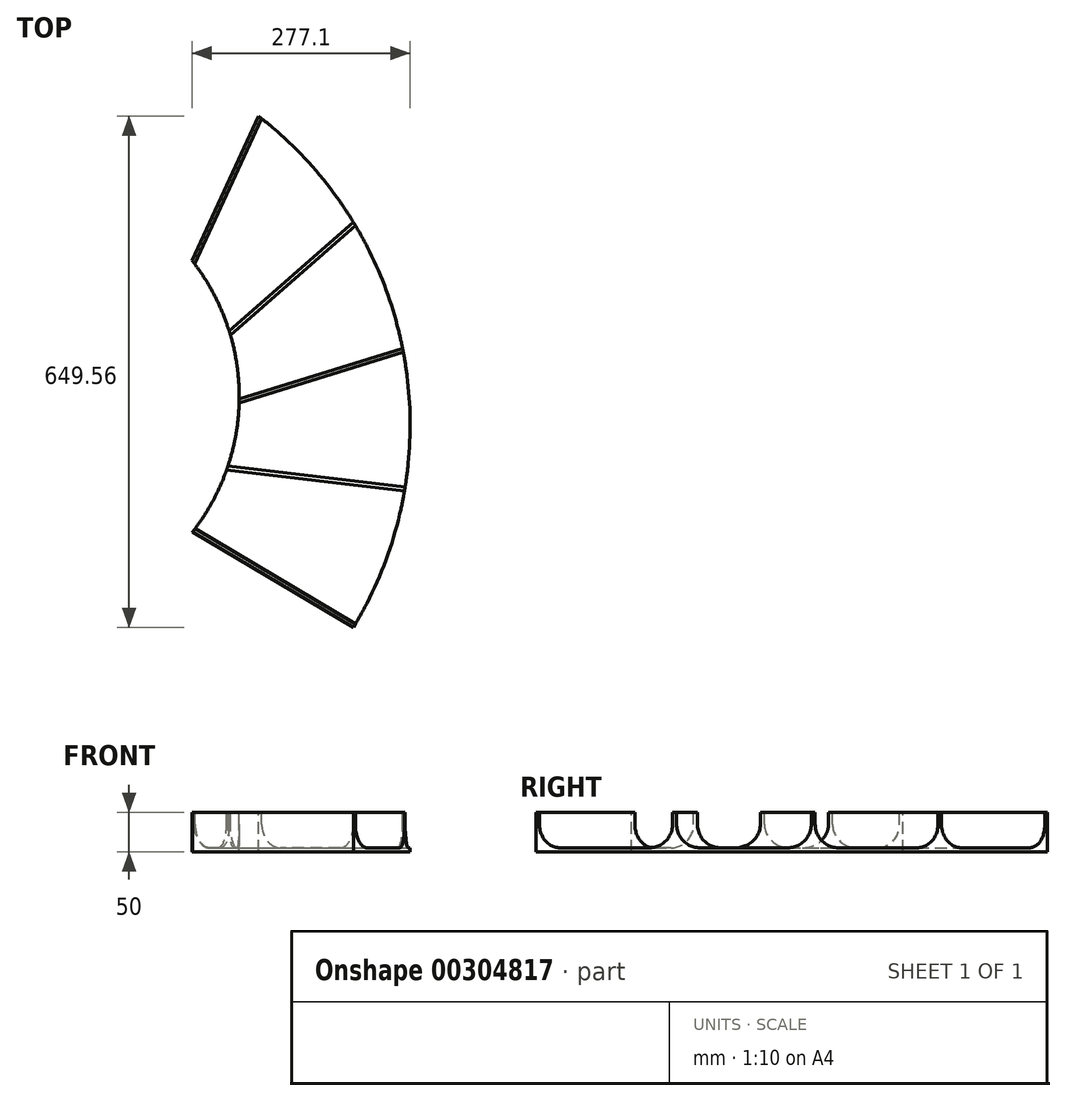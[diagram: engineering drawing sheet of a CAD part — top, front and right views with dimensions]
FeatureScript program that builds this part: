
annotation { "Feature Type Name" : "Feature", "Feature Type Description" : "" }
export const myFeature = defineFeature(function(context is Context, id is Id, definition is map)
    precondition{}
    {
        {
            var Q0;
            Q0=qCreatedBy(makeId("Top.planeOp"),FACE);
            var sketch = newSketch(context, id + "F0", { "sketchPlane" : qUnion([Q0])});
            skLineSegment(sketch, "E0.8.0", {"start": v(150, -96.9) * mm, "end": v(419.17, -128.76) * mm});
            skLineSegment(sketch, "E0.8.1", {"start": v(150, -174.88) * mm, "end": v(356.74, -297.88) * mm});
            skLineSegment(sketch, "E0.9.0", {"start": v(150, -35.73) * mm, "end": v(417.73, 47.4) * mm});
            skLineSegment(sketch, "E0.9.1", {"start": v(150, -91.87) * mm, "end": v(420, -123.83) * mm});
            skLineSegment(sketch, "E0.10.0", {"start": v(150, 27) * mm, "end": v(356.85, 208.4) * mm});
            skLineSegment(sketch, "E0.10.1", {"start": v(150, -30.5) * mm, "end": v(416.77, 52.34) * mm});
            skLineSegment(sketch, "E0.11.0", {"start": v(150, 153.59) * mm, "end": v(237.87, 344.2) * mm});
            skLineSegment(sketch, "E0.11.1", {"start": v(150, 33.65) * mm, "end": v(354.23, 212.75) * mm});
            skArc(sketch, "E1", {"start": v(356.74, -297.88) * mm, "mid": v(418.09, 45.52) * mm, "end": v(237.87, 344.2) * mm});
            skLineSegment(sketch, "E2", {"start": v(233.83, 347.38) * mm, "end": v(149.26, 163.92) * mm});
            skLineSegment(sketch, "E3", {"start": v(150.05, -180.73) * mm, "end": v(354.18, -302.18) * mm});
            skLineSegment(sketch, "E4", {"start": v(237.87, 344.2) * mm, "end": v(233.83, 347.38) * mm});
            skLineSegment(sketch, "E5", {"start": v(356.74, -297.88) * mm, "end": v(354.18, -302.18) * mm});
            skArc(sketch, "E6", {"start": v(150.05, -180.73) * mm, "mid": v(209.25, -8.27) * mm, "end": v(149.26, 163.92) * mm});
            skPoint(sketch, "E7", {"position": v(0, 0) * mm});
            skSolve(sketch);
        }
        {
            var Q0;
            Q0 = qSketchRegion(id + "F0", true);
            extrude(context, id + "F1", {"entities" : qUnion([Q0]), "oppositeDirection" : true, "depth" : 50 * mm});
        }
        {
            var Q0;
            {var subQ0=sQuery(id+"F0.wireOp",EDGE,"E0.8.0");Q0=makeQuery(id+"F0.imprint","IMPRINT",FACE,{"disambiguationData":[TD([[makeQuery(id+"F0.imprint","IMPRINT",EDGE,{"derivedFrom":subQ0}),-1.0]])]});}
            var Q1;
            {var subQ0=sQuery(id+"F0.wireOp",EDGE,"E0.9.0");Q1=makeQuery(id+"F0.imprint","IMPRINT",FACE,{"disambiguationData":[TD([[makeQuery(id+"F0.imprint","IMPRINT",EDGE,{"derivedFrom":subQ0}),-1.0]])]});}
            var Q2;
            {var subQ0=sQuery(id+"F0.wireOp",EDGE,"E0.10.0");Q2=makeQuery(id+"F0.imprint","IMPRINT",FACE,{"disambiguationData":[TD([[makeQuery(id+"F0.imprint","IMPRINT",EDGE,{"derivedFrom":subQ0}),-1.0]])]});}
            var Q3;
            {var subQ0=sQuery(id+"F0.wireOp",EDGE,"E0.11.0");Q3=makeQuery(id+"F0.imprint","IMPRINT",FACE,{"disambiguationData":[TD([[makeQuery(id+"F0.imprint","IMPRINT",EDGE,{"derivedFrom":subQ0}),-1.0]])]});}
            extrude(context, id + "F2", {"entities" : qUnion([Q0, Q1, Q2, Q3]), "operationType" : NewBodyOperationType.REMOVE, "oppositeDirection" : true, "depth" : 45 * mm});
        }
        {
            var Q0;
            Q0=makeQuery(id+"F2.boolean.opBoolean","COPY",EDGE,{"derivedFrom":makeQuery(id+"F2.opExtrude","CAP_EDGE",EDGE,{"disambiguationData":[OSD([sQuery(id+"F0.wireOp",EDGE,"E0.11.0")])],"isStart":false})});
            var Q1;
            Q1=makeQuery(id+"F2.boolean.opBoolean","COPY",EDGE,{"derivedFrom":makeQuery(id+"F2.opExtrude","CAP_EDGE",EDGE,{"disambiguationData":[OSD([sQuery(id+"F0.wireOp",EDGE,"E0.11.1")])],"isStart":false})});
            var Q2;
            Q2=makeQuery(id+"F2.boolean.opBoolean","COPY",EDGE,{"derivedFrom":makeQuery(id+"F2.opExtrude","CAP_EDGE",EDGE,{"disambiguationData":[OSD([sQuery(id+"F0.wireOp",EDGE,"E0.10.1")])],"isStart":false})});
            var Q3;
            Q3=makeQuery(id+"F2.boolean.opBoolean","COPY",EDGE,{"derivedFrom":makeQuery(id+"F2.opExtrude","CAP_EDGE",EDGE,{"disambiguationData":[OSD([sQuery(id+"F0.wireOp",EDGE,"E0.9.1")])],"isStart":false})});
            var Q4;
            Q4=makeQuery(id+"F2.boolean.opBoolean","COPY",EDGE,{"derivedFrom":makeQuery(id+"F2.opExtrude","CAP_EDGE",EDGE,{"disambiguationData":[OSD([sQuery(id+"F0.wireOp",EDGE,"E0.8.1")])],"isStart":false})});
            var Q5;
            Q5=makeQuery(id+"F2.boolean.opBoolean","COPY",EDGE,{"derivedFrom":makeQuery(id+"F2.opExtrude","CAP_EDGE",EDGE,{"disambiguationData":[OSD([sQuery(id+"F0.wireOp",EDGE,"E0.10.0")])],"isStart":false})});
            var Q6;
            Q6=makeQuery(id+"F2.boolean.opBoolean","COPY",EDGE,{"derivedFrom":makeQuery(id+"F2.opExtrude","CAP_EDGE",EDGE,{"disambiguationData":[OSD([sQuery(id+"F0.wireOp",EDGE,"E0.9.0")])],"isStart":false})});
            var Q7;
            Q7=makeQuery(id+"F2.boolean.opBoolean","COPY",EDGE,{"derivedFrom":makeQuery(id+"F2.opExtrude","CAP_EDGE",EDGE,{"disambiguationData":[OSD([sQuery(id+"F0.wireOp",EDGE,"E0.8.0")])],"isStart":false})});
            fillet(context, id + "F3", {"entities" : qUnion([Q0, Q1, Q2, Q3, Q4, Q5, Q6, Q7]), "radius" : 30 * mm, "tangentPropagation" : true, "allowEdgeOverflow" : false});
        }
    });
